# Revit family: SC 2521 SMD
name_source: partatom
category: Lighting Fixtures
revit_build: Autodesk Revit 2017 (Build: 20160225_1515(x64)
units: mm (PartAtom-declared; Revit-internal decimal feet)

## family parameters
Cut with Voids When Loaded = No
Host = Face
Light Source = Yes
Part Type = Normal
Room Calculation Point = No
Round Connector Dimension = Use Diameter
Shared = No

## types (6) — shared parameters
Color Filter = 16777215
Default Elevation = 1219 mm
Description = PENDANT - MICRO LENS (DIRECT)
Dimming Lamp Color Temperature Shift = <None>
Emit Shape Visible in Rendering = Yes
Emit from Rectangle Length = 49 mm  [stored 0.160761 ft]
Emit from Rectangle Width = 2521 mm  [stored 8.271 ft]
Lamp = LED
Manufacturer = ARLIGHT
Model = SC2521SMD
Tilt Angle = 90.00°
Type Comments = STELLA-CONT-END
Type Image = stella_black_pendant.png

## per-type parameters (varying)
| type | Apparent Load | Photometric Web File | Wattage Comments |
| SCSMD.2521.40.40 | 40 VA | SC 2521 SMD-40W-4K(SG-120mA).IES | 40 |
| SCSMD.2521.40.30 | 40 VA | SC 2521 SMD-40W-3K(SG-120mA).IES | 40 |
| SCSMD.2521.68.30 | 68 VA | SC 2521 SMD-68W-3K(SG-200mA).IES | 68 |
| SCSMD.2521.68.40 | 68 VA | SC 2521 SMD-68W-4K(SG-200mA).IES | 68 |
| SCSMD.2521.115.30 | 115 VA | SC 2521 SMD-115W-3K(SG-350mA).IES | 115 |
| SCSMD.2521.115.40 | 115 VA | SC 2521 SMD-115W-4K(SG-350mA).IES | 115 |

note: [stored X ft] marks values corroborated as IEEE doubles in the binary element streams (Revit-internal decimal feet)

## geometry (parser evidence)
native form markers: Sweep x1
no freeform markers — native parametric forms only
